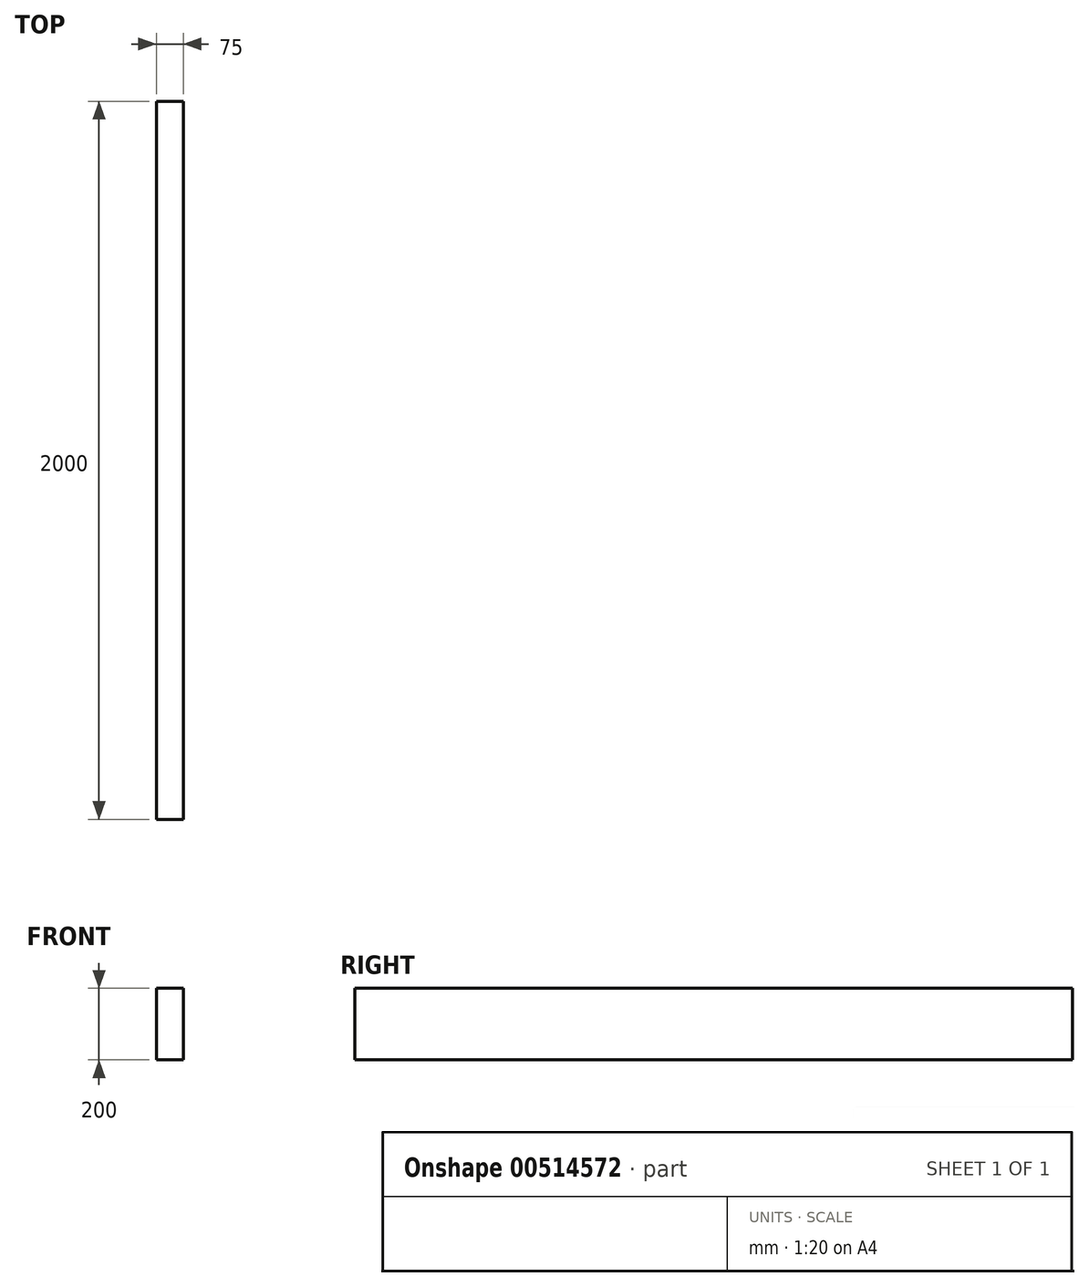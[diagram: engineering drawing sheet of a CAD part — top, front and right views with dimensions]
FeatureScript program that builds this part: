
annotation { "Feature Type Name" : "Feature", "Feature Type Description" : "" }
export const myFeature = defineFeature(function(context is Context, id is Id, definition is map)
    precondition{}
    {
        {
            var Q0;
            Q0=qCreatedBy(makeId("Front.planeOp"),FACE);
            var sketch = newSketch(context, id + "F0", { "sketchPlane" : qUnion([Q0])});
            skLineSegment(sketch, "E0.bottom", {"start": v(37.5, 100) * mm, "end": v(-37.5, 100) * mm});
            skLineSegment(sketch, "E0.top", {"start": v(37.5, -100) * mm, "end": v(-37.5, -100) * mm});
            skLineSegment(sketch, "E0.left", {"start": v(37.5, 100) * mm, "end": v(37.5, -100) * mm});
            skLineSegment(sketch, "E0.right", {"start": v(-37.5, 100) * mm, "end": v(-37.5, -100) * mm});
            skPoint(sketch, "E0.middle", {"position": v(0, 0) * mm});
            skSolve(sketch);
        }
        {
            var Q0;
            Q0 = qSketchRegion(id + "F0", true);
            extrude(context, id + "F1", {"entities" : qUnion([Q0]), "depth" : 2000 * mm, "offsetDistance" : 25 * mm});
        }
    });
